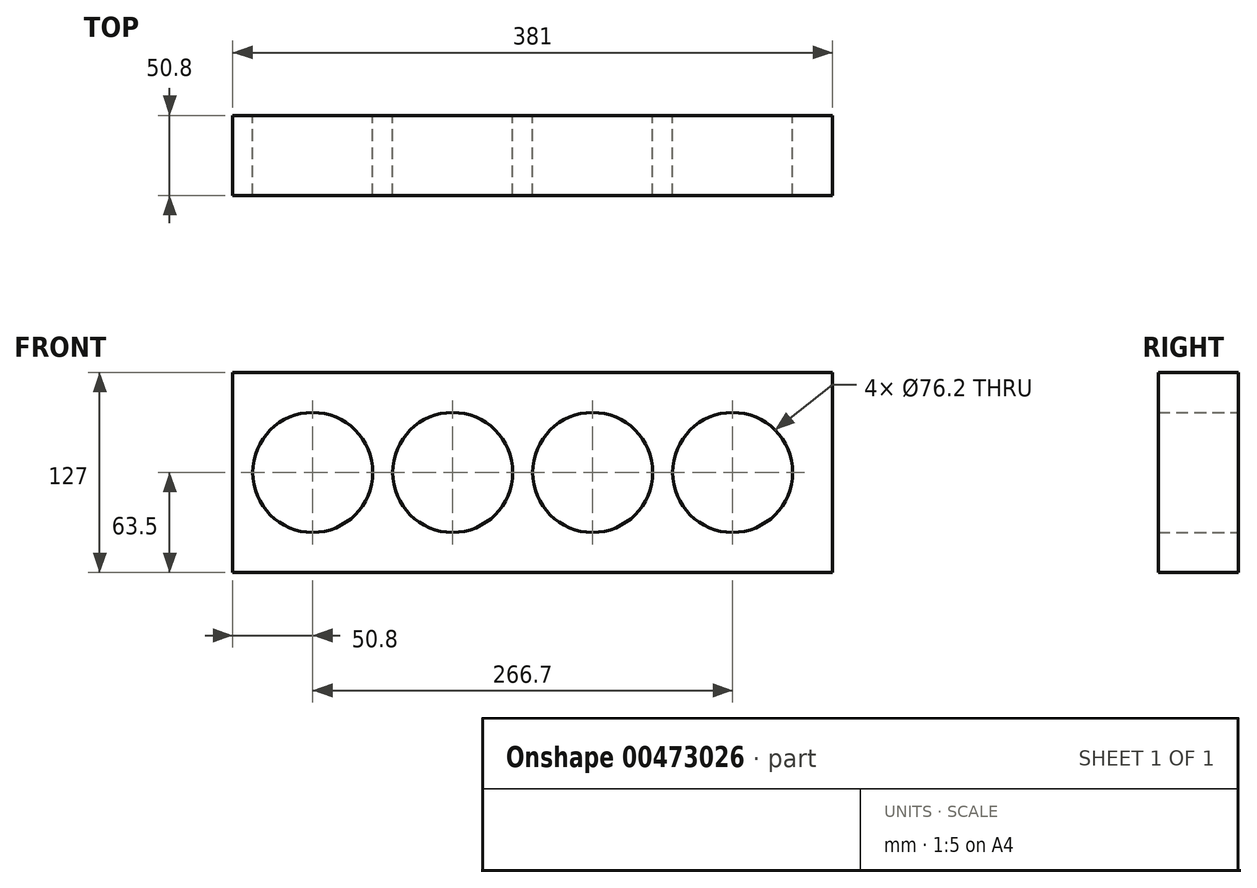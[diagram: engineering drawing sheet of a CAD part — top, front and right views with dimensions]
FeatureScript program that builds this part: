
annotation { "Feature Type Name" : "Feature", "Feature Type Description" : "" }
export const myFeature = defineFeature(function(context is Context, id is Id, definition is map)
    precondition{}
    {
        {
            var Q0;
            Q0=qCreatedBy(makeId("Front.planeOp"),FACE);
            var sketch = newSketch(context, id + "F0", { "sketchPlane" : qUnion([Q0])});
            skLineSegment(sketch, "E0.bottom", {"start": v(190.5, 63.5) * mm, "end": v(-190.5, 63.5) * mm});
            skLineSegment(sketch, "E0.top", {"start": v(190.5, -63.5) * mm, "end": v(-190.5, -63.5) * mm});
            skLineSegment(sketch, "E0.left", {"start": v(190.5, 63.5) * mm, "end": v(190.5, -63.5) * mm});
            skLineSegment(sketch, "E0.right", {"start": v(-190.5, 63.5) * mm, "end": v(-190.5, -63.5) * mm});
            skPoint(sketch, "E0.middle", {"position": v(0, 0) * mm});
            skCircle(sketch, "E1", {"center": v(-139.7, 0) * mm, "radius": 38.1 * mm});
            skCircle(sketch, "E2", {"center": v(-50.8, 0) * mm, "radius": 38.1 * mm});
            skCircle(sketch, "E3", {"center": v(38.1, 0) * mm, "radius": 38.1 * mm});
            skCircle(sketch, "E4", {"center": v(127, 0) * mm, "radius": 38.1 * mm});
            skSolve(sketch);
        }
        {
            var Q0;
            Q0=makeQuery(id+"F0.imprint","IMPRINT",FACE,{"disambiguationData":[TD([[makeQuery(id+"F0.imprint","IMPRINT",EDGE,{"derivedFrom":sQuery(id+"F0.wireOp",EDGE,"E0.bottom")}),1.0]])]});
            extrude(context, id + "F1", {"entities" : qUnion([Q0]), "depth" : 50.8 * mm});
        }
    });
